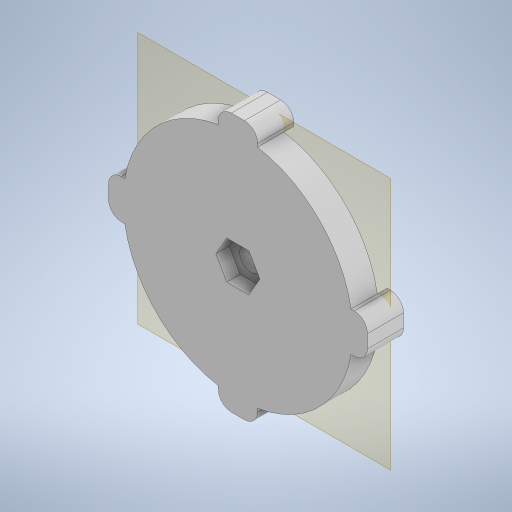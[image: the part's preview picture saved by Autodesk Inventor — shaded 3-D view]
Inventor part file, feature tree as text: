
AUTODESK INVENTOR PART (.ipt)
format: ipt  version: 2023 (Build 270158000, 158)  size: 454,656 bytes
history: native  units: in
note: dims shown in document units (in); Inventor stores cm internally (conversion verified against a paired STEP export)
features: projected_geometry x11, extrude x8, sketch x8, reference x6, other x5
ambient origin geometry x8: Origin, YZ Plane, XZ Plane, XY Plane, X Axis, Y Axis, Z Axis, Center Point
bodies: Body1 (feature_tree)
feature tree (38):
  other  "Bryła1"
  other  "Płaszczyzna konstrukcyjna1"
  extrude  "Wyciągnięcie proste1"  Depth=0.1575in TaperAngle=0.0deg
  extrude  "Wyciągnięcie proste2"  Depth=0.0079in
  extrude  "Wyciągnięcie proste3"  Depth=0.0591in TaperAngle=0.0deg
  extrude  "Wyciągnięcie proste4"  TaperAngle=0.0deg  [1 undecoded]
  extrude  "Wyciągnięcie proste5"  Depth=0.3937in TaperAngle=0.0deg
  extrude  "Wyciągnięcie proste6"  Depth=0.3937in TaperAngle=0.0deg
  extrude  "Wyciągnięcie proste7"  Depth=0.2283in
  extrude  "Wyciągnięcie proste8"  Depth=0.0787in TaperAngle=0.0deg
  sketch  "Szkic1"
  reference  "Odniesienie1"
  reference  "Odniesienie2"
  reference  "Odniesienie3"
  reference  "Odniesienie4"
  sketch  "Szkic2"
  reference  "Odniesienie5"
  reference  "Odniesienie6"
  sketch  "Szkic3"
  projected_geometry  "Pętla rzutowana1"
  projected_geometry  "Pętla rzutowana2"
  projected_geometry  "Pętla rzutowana3"
  projected_geometry  "Pętla rzutowana4"
  sketch  "Szkic4"
  projected_geometry  "Pętla rzutowana5"
  projected_geometry  "Pętla rzutowana6"
  projected_geometry  "Pętla rzutowana7"
  projected_geometry  "Pętla rzutowana8"
  sketch  "Szkic5"
  projected_geometry  "Pętla rzutowana9"
  sketch  "Szkic6"
  sketch  "Szkic7"
  projected_geometry  "Pętla rzutowana10"
  sketch  "Szkic8"
  projected_geometry  "Pętla rzutowana11"
  other  "Zespół2"
  other  "podstawa_formy:1"
  other  "gora:1"
note: 1 required parameter value undecoded (feature->parameter linkage not recoverable at this tier; creation-order binding heuristic only, values carry confidence <= 0.55)
